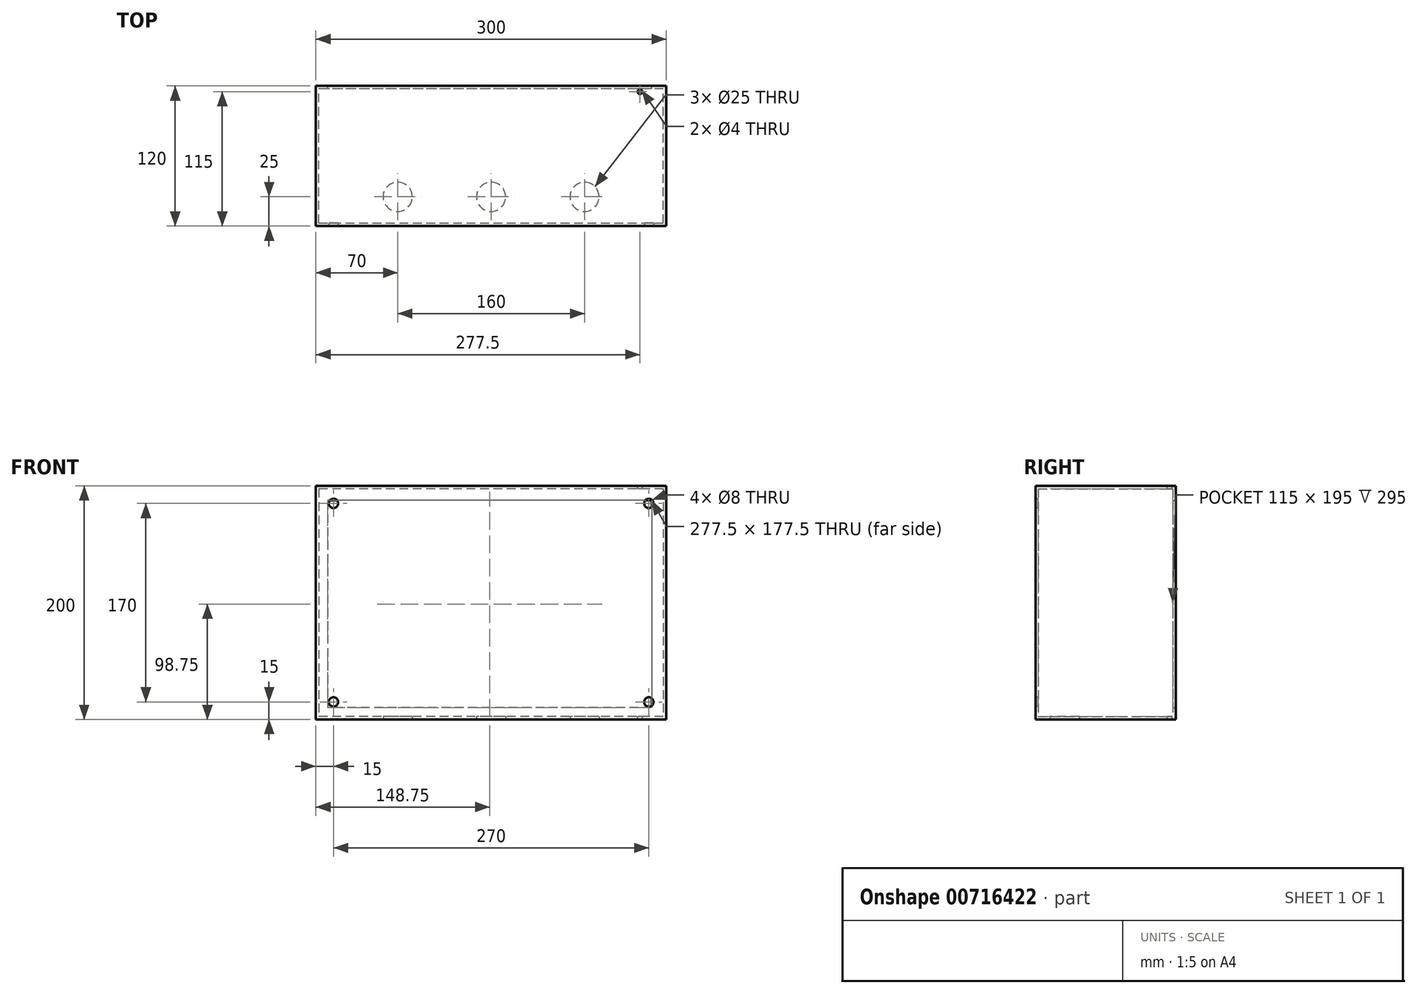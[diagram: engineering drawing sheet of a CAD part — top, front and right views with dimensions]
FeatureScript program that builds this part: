
annotation { "Feature Type Name" : "Feature", "Feature Type Description" : "" }
export const myFeature = defineFeature(function(context is Context, id is Id, definition is map)
    precondition{}
    {
        {
            var Q0;
            Q0=qCreatedBy(makeId("Top.planeOp"),FACE);
            var sketch = newSketch(context, id + "F0", { "sketchPlane" : qUnion([Q0])});
            skLineSegment(sketch, "E0.bottom", {"start": v(0, 0) * mm, "end": v(300, 0) * mm});
            skLineSegment(sketch, "E0.top", {"start": v(0, 120) * mm, "end": v(300, 120) * mm});
            skLineSegment(sketch, "E0.left", {"start": v(0, 0) * mm, "end": v(0, 120) * mm});
            skLineSegment(sketch, "E0.right", {"start": v(300, 0) * mm, "end": v(300, 120) * mm});
            skSolve(sketch);
        }
        {
            var Q0;
            Q0=qSketchRegion(id+"F0",true);
            extrude(context, id + "F1", {"entities" : qUnion([Q0]), "depth" : 200 * mm, "offsetDistance" : 25 * mm});
        }
        {
            var Q0;
            Q0=makeQuery(id+"F1.opExtrude","SWEPT_FACE",FACE,{"disambiguationData":[OSD([sQuery(id+"F0.wireOp",EDGE,"E0.top")])]});
            shell(context, id + "F2", {"entities" : qUnion([Q0]), "thickness" : 2.5 * mm});
        }
        {
            var Q0;
            Q0=makeQuery(id+"F1.opExtrude","SWEPT_FACE",FACE,{"disambiguationData":[OSD([sQuery(id+"F0.wireOp",EDGE,"E0.top")])]});
            var sketch = newSketch(context, id + "F3", { "sketchPlane" : qUnion([Q0])});
            skLineSegment(sketch, "E1.bottom", {"start": v(-297.5, 197.5) * mm, "end": v(0, 197.5) * mm});
            skLineSegment(sketch, "E1.top", {"start": v(-297.5, 0) * mm, "end": v(0, 0) * mm});
            skLineSegment(sketch, "E1.left", {"start": v(-297.5, 197.5) * mm, "end": v(-297.5, 0) * mm});
            skLineSegment(sketch, "E1.right", {"start": v(0, 197.5) * mm, "end": v(0, 0) * mm});
            skLineSegment(sketch, "E2.0", {"start": v(-10, 187.5) * mm, "end": v(-10, 10) * mm});
            skLineSegment(sketch, "E2.1", {"start": v(-287.5, 187.5) * mm, "end": v(-10, 187.5) * mm});
            skLineSegment(sketch, "E2.2", {"start": v(-287.5, 187.5) * mm, "end": v(-287.5, 10) * mm});
            skLineSegment(sketch, "E2.3", {"start": v(-287.5, 10) * mm, "end": v(-10, 10) * mm});
            skSolve(sketch);
        }
        {
            var Q0;
            Q0=qSketchRegion(id+"F3",true);
            extrude(context, id + "F4", {"entities" : qUnion([Q0]), "operationType" : NewBodyOperationType.ADD, "oppositeDirection" : true, "depth" : 2.5 * mm, "offsetDistance" : 25 * mm});
        }
        {
            var Q0;
            Q0=makeQuery(id+"F1.opExtrude","CAP_FACE",FACE,{"disambiguationData":[OSD([sQuery(id+"F0.wireOp",EDGE,"E0.bottom"),sQuery(id+"F0.wireOp",EDGE,"E0.top"),sQuery(id+"F0.wireOp",EDGE,"E0.left"),sQuery(id+"F0.wireOp",EDGE,"E0.right")])],"isStart":false});
            var sketch = newSketch(context, id + "F5", { "sketchPlane" : qUnion([Q0])});
            skCircle(sketch, "E3", {"center": v(277.5, 115) * mm, "radius": 2 * mm});
            skSolve(sketch);
        }
        {
            var Q0;
            Q0=qSketchRegion(id+"F5",true);
            extrude(context, id + "F6", {"entities" : qUnion([Q0]), "operationType" : NewBodyOperationType.REMOVE, "endBound" : BoundingType.THROUGH_ALL, "oppositeDirection" : true, "depth" : 25 * mm, "offsetDistance" : 25 * mm});
        }
        {
            var Q0;
            Q0=makeQuery(id+"F1.opExtrude","SWEPT_FACE",FACE,{"disambiguationData":[OSD([sQuery(id+"F0.wireOp",EDGE,"E0.bottom")])]});
            var sketch = newSketch(context, id + "F7", { "sketchPlane" : qUnion([Q0])});
            skCircle(sketch, "E4", {"center": v(285, 185) * mm, "radius": 4 * mm});
            skLineSegment(sketch, "E5", {"start": v(300, 100) * mm, "end": v(0, 100) * mm, "construction": true});
            skLineSegment(sketch, "E6", {"start": v(150, 0) * mm, "end": v(150, 200) * mm, "construction": true});
            skCircle(sketch, "E7.MirrorC", {"center": v(285, 15) * mm, "radius": 4 * mm});
            skCircle(sketch, "E8.MirrorC", {"center": v(15, 185) * mm, "radius": 4 * mm});
            skCircle(sketch, "E9.MirrorC", {"center": v(15, 15) * mm, "radius": 4 * mm});
            skSolve(sketch);
        }
        {
            var Q0;
            Q0=qSketchRegion(id+"F7",true);
            extrude(context, id + "F8", {"entities" : qUnion([Q0]), "operationType" : NewBodyOperationType.REMOVE, "oppositeDirection" : true, "depth" : 2.5 * mm, "offsetDistance" : 25 * mm});
        }
        {
            var Q0;
            Q0=makeQuery(id+"F0.imprint","IMPRINT",FACE,{"disambiguationData":[TD([[makeQuery(id+"F0.imprint","IMPRINT",EDGE,{"derivedFrom":sQuery(id+"F0.wireOp",EDGE,"E0.bottom")}),1.0]])]});
            var sketch = newSketch(context, id + "F9", { "sketchPlane" : qUnion([Q0])});
            skCircle(sketch, "E10", {"center": v(70, 25) * mm, "radius": 12.5 * mm});
            skCircle(sketch, "E11.1.0.0", {"center": v(150, 25) * mm, "radius": 12.5 * mm});
            skCircle(sketch, "E11.2.0.0", {"center": v(230, 25) * mm, "radius": 12.5 * mm});
            skLineSegment(sketch, "E11.direction1", {"start": v(70, 25) * mm, "end": v(150, 25) * mm, "construction": true});
            skSolve(sketch);
        }
        {
            var Q0;
            Q0 = qSketchRegion(id + "F9", true);
            extrude(context, id + "F10", {"entities" : qUnion([Q0]), "operationType" : NewBodyOperationType.REMOVE, "depth" : 25 * mm, "offsetDistance" : 25 * mm});
        }
    });
